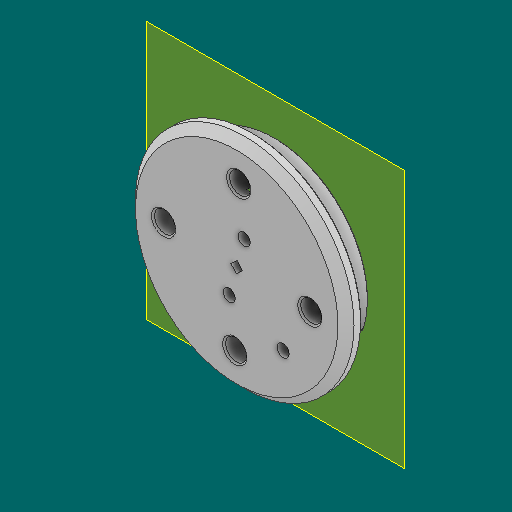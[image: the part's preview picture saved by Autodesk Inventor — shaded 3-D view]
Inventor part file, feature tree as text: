
AUTODESK INVENTOR PART (.ipt)
format: ipt  version: 2023.1 (Build 271208000, 208)  size: 245,248 bytes
history: native  units: in
note: dims shown in document units (in); Inventor stores cm internally (conversion verified against a paired STEP export)
features: sketch x6, other x3, plane x1
ambient origin geometry x8: Origin, YZ Plane, XZ Plane, XY Plane, X Axis, Y Axis, Z Axis, Center Point
bodies: Solid1 (feature_tree)
feature tree (10):
  other  "DiffCap_MIR.ipt"
  other  "Solid1::DiffCap_MIR.ipt"
  other  "TaggingFeature1"
  sketch  "Sketch1"  dims[d0=0.3937in]
  sketch  "Sketch2"
  sketch  "Sketch3"
  sketch  "Sketch4"
  sketch  "Sketch5"
  sketch  "Sketch6"
  plane  "Work Plane1"
